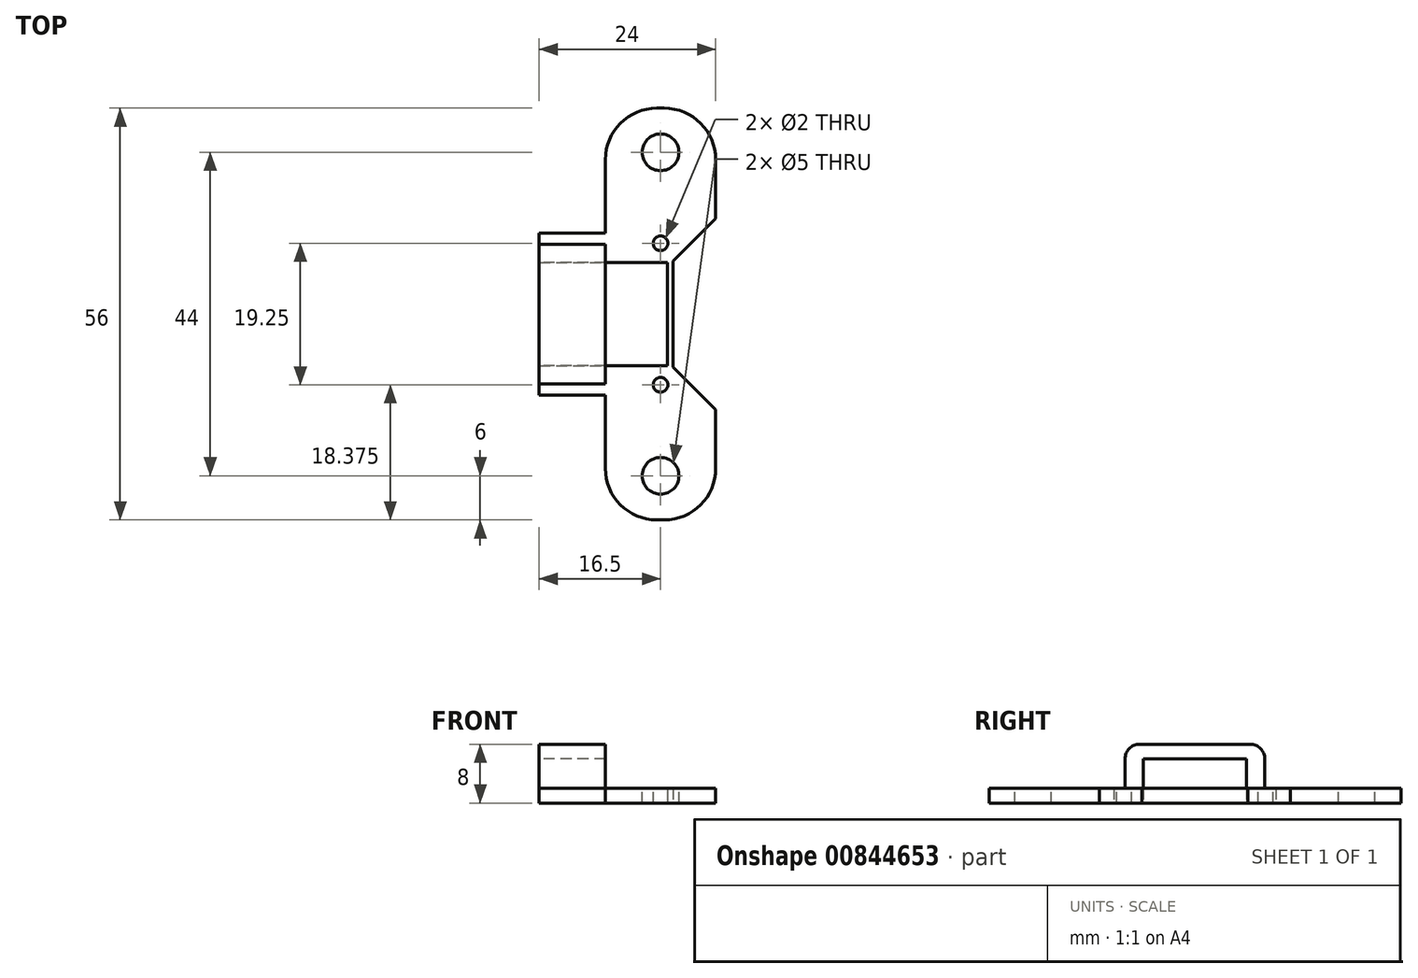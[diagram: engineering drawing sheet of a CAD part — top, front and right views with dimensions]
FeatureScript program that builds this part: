
annotation { "Feature Type Name" : "Feature", "Feature Type Description" : "" }
export const myFeature = defineFeature(function(context is Context, id is Id, definition is map)
    precondition{}
    {
        {
            var Q0;
            Q0=qCreatedBy(makeId("Top.planeOp"),FACE);
            var sketch = newSketch(context, id + "F0", { "sketchPlane" : qUnion([Q0])});
            skLineSegment(sketch, "E0.bottom", {"start": v(-7.5, 10.5) * mm, "end": v(7.5, 10.5) * mm});
            skLineSegment(sketch, "E0.top", {"start": v(-7.5, -10.5) * mm, "end": v(7.5, -10.5) * mm});
            skLineSegment(sketch, "E0.left", {"start": v(-7.5, 10.5) * mm, "end": v(-7.5, -10.5) * mm});
            skLineSegment(sketch, "E0.right", {"start": v(7.5, 10.5) * mm, "end": v(7.5, -10.5) * mm});
            skPoint(sketch, "E0.middle", {"position": v(0, 0) * mm});
            skLineSegment(sketch, "E1", {"start": v(16.54, 17.5) * mm, "end": v(-27.39, 17.5) * mm});
            skLineSegment(sketch, "E2", {"start": v(-2.72, 10.5) * mm, "end": v(-2.52, 10.5) * mm});
            skLineSegment(sketch, "E3", {"start": v(-2.72, 11.06) * mm, "end": v(-1.72, 10.5) * mm});
            skLineSegment(sketch, "E4.MirrorCS", {"start": v(-2.72, 23.94) * mm, "end": v(-1.72, 24.5) * mm});
            skLineSegment(sketch, "E5.MirrorCS", {"start": v(-2.72, 24.5) * mm, "end": v(-2.52, 24.5) * mm});
            skPoint(sketch, "E6.MirrorP", {"position": v(0, 35) * mm});
            skLineSegment(sketch, "E7.MirrorCS", {"start": v(-7.5, 45.5) * mm, "end": v(7.5, 45.5) * mm});
            skLineSegment(sketch, "E8.MirrorCS", {"start": v(-7.5, 24.5) * mm, "end": v(7.5, 24.5) * mm});
            skLineSegment(sketch, "E9.MirrorCS", {"start": v(-7.5, 24.5) * mm, "end": v(-7.5, 45.5) * mm});
            skLineSegment(sketch, "E10.MirrorCS", {"start": v(7.5, 24.5) * mm, "end": v(7.5, 45.5) * mm});
            skLineSegment(sketch, "E11", {"start": v(1.7, 10.5) * mm, "end": v(1.7, 24.5) * mm});
            skLineSegment(sketch, "E12", {"start": v(0.94, 10.5) * mm, "end": v(0.94, 24.5) * mm});
            skSolve(sketch);
        }
        {
            var Q0;
            Q0=qSketchRegion(id+"F0",true);
            extrude(context, id + "F1", {"entities" : qUnion([Q0]), "depth" : 2 * mm, "offsetDistance" : 25 * mm});
        }
        {
            var Q0;
            Q0=makeQuery(id+"F1.opExtrude","SWEPT_EDGE",EDGE,{"disambiguationData":[OSD([sQuery(id+"F0.wireOp",EDGE,"E0.top"),sQuery(id+"F0.wireOp",EDGE,"E0.left")])]});
            var Q1;
            Q1=makeQuery(id+"F1.opExtrude","SWEPT_EDGE",EDGE,{"disambiguationData":[OSD([sQuery(id+"F0.wireOp",EDGE,"E0.top"),sQuery(id+"F0.wireOp",EDGE,"E0.right")])]});
            var Q2;
            Q2=makeQuery(id+"F1.opExtrude","SWEPT_EDGE",EDGE,{"disambiguationData":[OSD([sQuery(id+"F0.wireOp",EDGE,"4d69a73c-c125-441b-aeee-6358f9a7b48c0.MirrorCS"),sQuery(id+"F0.wireOp",EDGE,"4d69a73c-c125-441b-aeee-6358f9a7b48c3.MirrorCS")])]});
            var Q3;
            Q3=makeQuery(id+"F1.opExtrude","SWEPT_EDGE",EDGE,{"disambiguationData":[OSD([sQuery(id+"F0.wireOp",EDGE,"4d69a73c-c125-441b-aeee-6358f9a7b48c1.MirrorCS"),sQuery(id+"F0.wireOp",EDGE,"4d69a73c-c125-441b-aeee-6358f9a7b48c3.MirrorCS")])]});
            var Q4;
            Q4=makeQuery(id+"F1.opExtrude","SWEPT_EDGE",EDGE,{"disambiguationData":[OSD([sQuery(id+"F0.wireOp",EDGE,"E7.MirrorCS"),sQuery(id+"F0.wireOp",EDGE,"E10.MirrorCS")])]});
            var Q5;
            Q5=makeQuery(id+"F1.opExtrude","SWEPT_EDGE",EDGE,{"disambiguationData":[OSD([sQuery(id+"F0.wireOp",EDGE,"E7.MirrorCS"),sQuery(id+"F0.wireOp",EDGE,"E9.MirrorCS")])]});
            fillet(context, id + "F2", {"entities" : qUnion([Q0, Q1, Q2, Q3, Q4, Q5]), "radius" : 7 * mm, "tangentPropagation" : true, "allowEdgeOverflow" : false});
        }
        {
            var Q0;
            Q0=makeQuery(id+"F1.opExtrude","CAP_FACE",FACE,{"disambiguationData":[OSD([sQuery(id+"F0.wireOp",EDGE,"E0.bottom"),sQuery(id+"F0.wireOp",EDGE,"E0.top"),sQuery(id+"F0.wireOp",EDGE,"E0.left"),sQuery(id+"F0.wireOp",EDGE,"E0.right")])],"isStart":false});
            var sketch = newSketch(context, id + "F3", { "sketchPlane" : qUnion([Q0])});
            skCircle(sketch, "E13", {"center": v(0, -4.5) * mm, "radius": 2.5 * mm});
            skLineSegment(sketch, "E14", {"start": v(0, -10.5) * mm, "end": v(0, -4.5) * mm});
            skLineSegment(sketch, "E15", {"start": v(4.6, 10.5) * mm, "end": v(4.6, 17) * mm});
            skLineSegment(sketch, "E16", {"start": v(19.61, 17) * mm, "end": v(-16.13, 17) * mm});
            skLineSegment(sketch, "E17", {"start": v(0, -4.5) * mm, "end": v(0, 7.87) * mm});
            skCircle(sketch, "E18", {"center": v(0, 7.87) * mm, "radius": 1 * mm});
            skLineSegment(sketch, "E19", {"start": v(0, 45.5) * mm, "end": v(0, 39.5) * mm});
            skCircle(sketch, "E20", {"center": v(0, 39.5) * mm, "radius": 2.5 * mm});
            skLineSegment(sketch, "E21", {"start": v(0, 39.5) * mm, "end": v(0, 27.12) * mm});
            skCircle(sketch, "E22", {"center": v(0, 27.12) * mm, "radius": 1 * mm});
            skSolve(sketch);
        }
        {
            var Q0;
            Q0=qSketchRegion(id+"F3",true);
            extrude(context, id + "F4", {"entities" : qUnion([Q0]), "operationType" : NewBodyOperationType.REMOVE, "endBound" : BoundingType.UP_TO_NEXT, "oppositeDirection" : true, "depth" : 25 * mm, "offsetDistance" : 25 * mm});
        }
        {
            var Q0;
            Q0=makeQuery(id+"F1.opExtrude","SWEPT_FACE",FACE,{"disambiguationData":[OSD([sQuery(id+"F0.wireOp",EDGE,"E0.left")])]});
            var sketch = newSketch(context, id + "F5", { "sketchPlane" : qUnion([Q0])});
            skLineSegment(sketch, "E23.bottom", {"start": v(-10.5, 2) * mm, "end": v(-6.5, 2) * mm});
            skLineSegment(sketch, "E23.top", {"start": v(-10.5, 0) * mm, "end": v(-6.5, 0) * mm});
            skLineSegment(sketch, "E23.left", {"start": v(-10.5, 2) * mm, "end": v(-10.5, 0) * mm});
            skLineSegment(sketch, "E23.right", {"start": v(-6.5, 2) * mm, "end": v(-6.5, 0) * mm});
            skSolve(sketch);
        }
        {
            var Q0;
            Q0=makeQuery(id+"F5.imprint","IMPRINT",FACE,{"disambiguationData":[TD([[makeQuery(id+"F5.imprint","IMPRINT",EDGE,{"derivedFrom":sQuery(id+"F5.wireOp",EDGE,"E23.bottom")}),-1.0]])]});
            var Q1;
            Q1=makeQuery(id+"F5.imprint","IMPRINT",FACE,{"disambiguationData":[TD([[makeQuery(id+"F5.imprint","IMPRINT",EDGE,{"derivedFrom":sQuery(id+"F5.wireOp",EDGE,"b54e5eb9-cc67-4eb8-8262-082db1211d390.MirrorCS")}),-1.0]])]});
            extrude(context, id + "F6", {"entities" : qUnion([Q0, Q1]), "operationType" : NewBodyOperationType.ADD, "depth" : 9 * mm, "offsetDistance" : 25 * mm});
        }
        {
            var Q0;
            Q0=makeQuery(id+"F6.boolean.opBoolean","MERGE",FACE,{"derivedFrom":[makeQuery(id+"F1.opExtrude","CAP_FACE",FACE,{"disambiguationData":[OSD([sQuery(id+"F0.wireOp",EDGE,"E0.bottom"),sQuery(id+"F0.wireOp",EDGE,"E0.top"),sQuery(id+"F0.wireOp",EDGE,"E0.left"),sQuery(id+"F0.wireOp",EDGE,"E0.right")])],"isStart":false}),makeQuery(id+"F6.opExtrude","SWEPT_FACE",FACE,{"disambiguationData":[OSD([sQuery(id+"F5.wireOp",EDGE,"E23.bottom")])]})]});
            var sketch = newSketch(context, id + "F7", { "sketchPlane" : qUnion([Q0])});
            skLineSegment(sketch, "E24.bottom", {"start": v(-16.5, 10.5) * mm, "end": v(-7.5, 10.5) * mm});
            skLineSegment(sketch, "E24.top", {"start": v(-16.5, 8) * mm, "end": v(-7.5, 8) * mm});
            skLineSegment(sketch, "E24.left", {"start": v(-16.5, 10.5) * mm, "end": v(-16.5, 8) * mm});
            skLineSegment(sketch, "E24.right", {"start": v(-7.5, 10.5) * mm, "end": v(-7.5, 8) * mm});
            skLineSegment(sketch, "E25", {"start": v(-8.07, 10.5) * mm, "end": v(-8.07, 17) * mm});
            skLineSegment(sketch, "E26", {"start": v(-3.29, 17) * mm, "end": v(-20.76, 17) * mm});
            skSolve(sketch);
        }
        {
            var Q0;
            Q0=makeQuery(id+"F7.imprint","IMPRINT",FACE,{"disambiguationData":[TD([[makeQuery(id+"F7.imprint","IMPRINT",EDGE,{"derivedFrom":sQuery(id+"F7.wireOp",EDGE,"E24.bottom")}),-1.0]])]});
            var Q1;
            Q1=makeQuery(id+"F7.imprint","IMPRINT",FACE,{"disambiguationData":[TD([[makeQuery(id+"F7.imprint","IMPRINT",EDGE,{"derivedFrom":sQuery(id+"F7.wireOp",EDGE,"8816faac-e9ce-4b0a-a729-0d2c297b35d70.MirrorCS")}),1.0]])]});
            extrude(context, id + "F8", {"entities" : qUnion([Q0, Q1]), "operationType" : NewBodyOperationType.ADD, "depth" : 6 * mm, "offsetDistance" : 25 * mm});
        }
        {
            var Q0;
            Q0=makeQuery(id+"F8.boolean.opBoolean","MERGE",FACE,{"derivedFrom":[makeQuery(id+"F6.boolean.opBoolean","MERGE",FACE,{"derivedFrom":[makeQuery(id+"F1.opExtrude","SWEPT_FACE",FACE,{"disambiguationData":[OSD([sQuery(id+"F0.wireOp",EDGE,"E0.bottom")])]}),makeQuery(id+"F6.opExtrude","SWEPT_FACE",FACE,{"disambiguationData":[OSD([sQuery(id+"F5.wireOp",EDGE,"E23.left")])]})]}),makeQuery(id+"F8.opExtrude","SWEPT_FACE",FACE,{"disambiguationData":[OSD([sQuery(id+"F7.wireOp",EDGE,"E24.bottom")])]})]});
            var sketch = newSketch(context, id + "F9", { "sketchPlane" : qUnion([Q0])});
            skLineSegment(sketch, "E27.bottom", {"start": v(7.5, 8) * mm, "end": v(16.5, 8) * mm});
            skLineSegment(sketch, "E27.top", {"start": v(7.5, 6) * mm, "end": v(16.5, 6) * mm});
            skLineSegment(sketch, "E27.left", {"start": v(7.5, 8) * mm, "end": v(7.5, 6) * mm});
            skLineSegment(sketch, "E27.right", {"start": v(16.5, 8) * mm, "end": v(16.5, 6) * mm});
            skSolve(sketch);
        }
        {
            var Q0;
            Q0 = qSketchRegion(id + "F9", true);
            extrude(context, id + "F10", {"entities" : qUnion([Q0]), "operationType" : NewBodyOperationType.ADD, "depth" : 14 * mm, "offsetDistance" : 25 * mm});
        }
        {
            var Q0;
            Q0=makeQuery(id+"F1.opExtrude","SWEPT_FACE",FACE,{"disambiguationData":[OSD([sQuery(id+"F0.wireOp",EDGE,"E9.MirrorCS")])]});
            var sketch = newSketch(context, id + "F11", { "sketchPlane" : qUnion([Q0])});
            skLineSegment(sketch, "E28.bottom", {"start": v(-24.5, 2) * mm, "end": v(-28.5, 2) * mm});
            skLineSegment(sketch, "E28.top", {"start": v(-24.5, 0) * mm, "end": v(-28.5, 0) * mm});
            skLineSegment(sketch, "E28.left", {"start": v(-24.5, 2) * mm, "end": v(-24.5, 0) * mm});
            skLineSegment(sketch, "E28.right", {"start": v(-28.5, 2) * mm, "end": v(-28.5, 0) * mm});
            skSolve(sketch);
        }
        {
            var Q0;
            Q0=makeQuery(id+"F11.imprint","IMPRINT",FACE,{"disambiguationData":[TD([[makeQuery(id+"F11.imprint","IMPRINT",EDGE,{"derivedFrom":sQuery(id+"F11.wireOp",EDGE,"E28.bottom")}),1.0]])]});
            extrude(context, id + "F12", {"entities" : qUnion([Q0]), "operationType" : NewBodyOperationType.ADD, "depth" : 9 * mm, "offsetDistance" : 25 * mm});
        }
        {
            var Q0;
            Q0=makeQuery(id+"F12.boolean.opBoolean","MERGE",FACE,{"derivedFrom":[makeQuery(id+"F6.boolean.opBoolean","MERGE",FACE,{"derivedFrom":[makeQuery(id+"F1.opExtrude","CAP_FACE",FACE,{"disambiguationData":[OSD([sQuery(id+"F0.wireOp",EDGE,"E0.bottom"),sQuery(id+"F0.wireOp",EDGE,"E0.top"),sQuery(id+"F0.wireOp",EDGE,"E0.left"),sQuery(id+"F0.wireOp",EDGE,"E0.right"),sQuery(id+"F0.wireOp",EDGE,"4d69a73c-c125-441b-aeee-6358f9a7b48c0.MirrorCS"),sQuery(id+"F0.wireOp",EDGE,"4d69a73c-c125-441b-aeee-6358f9a7b48c1.MirrorCS"),sQuery(id+"F0.wireOp",EDGE,"4d69a73c-c125-441b-aeee-6358f9a7b48c2.MirrorCS"),sQuery(id+"F0.wireOp",EDGE,"4d69a73c-c125-441b-aeee-6358f9a7b48c3.MirrorCS"),sQuery(id+"F0.wireOp",EDGE,"g9jlqCbB-dlW6-GfCL-Cnde-qGy19OqoHRY9"),sQuery(id+"F0.wireOp",EDGE,"YbJINRbM-a1Qn-wjUW-cin5-VxgVwcj2AwoP")])],"isStart":false}),makeQuery(id+"F6.opExtrude","SWEPT_FACE",FACE,{"disambiguationData":[OSD([sQuery(id+"F5.wireOp",EDGE,"E23.bottom")])]})]}),makeQuery(id+"F12.opExtrude","SWEPT_FACE",FACE,{"disambiguationData":[OSD([sQuery(id+"F11.wireOp",EDGE,"fP8b6zdj-eh1C-UePH-MVhF-EP79czhgLk8B.bottom")])]})]});
            var sketch = newSketch(context, id + "F13", { "sketchPlane" : qUnion([Q0])});
            skLineSegment(sketch, "E29.bottom", {"start": v(-16.5, 24.5) * mm, "end": v(-7.5, 24.5) * mm});
            skLineSegment(sketch, "E29.top", {"start": v(-16.5, 27) * mm, "end": v(-7.5, 27) * mm});
            skLineSegment(sketch, "E29.left", {"start": v(-16.5, 24.5) * mm, "end": v(-16.5, 27) * mm});
            skLineSegment(sketch, "E29.right", {"start": v(-7.5, 24.5) * mm, "end": v(-7.5, 27) * mm});
            skSolve(sketch);
        }
        {
            var Q0;
            Q0=makeQuery(id+"F13.imprint","IMPRINT",FACE,{"disambiguationData":[TD([[makeQuery(id+"F13.imprint","IMPRINT",EDGE,{"derivedFrom":sQuery(id+"F13.wireOp",EDGE,"E29.bottom")}),1.0]])]});
            extrude(context, id + "F14", {"entities" : qUnion([Q0]), "operationType" : NewBodyOperationType.ADD, "depth" : 6 * mm, "offsetDistance" : 25 * mm});
        }
        {
            var Q0;
            Q0=makeQuery(id+"F1.opExtrude","SWEPT_EDGE",EDGE,{"disambiguationData":[OSD([sQuery(id+"F0.wireOp",EDGE,"4d69a73c-c125-441b-aeee-6358f9a7b48c0.MirrorCS"),sQuery(id+"F0.wireOp",EDGE,"4d69a73c-c125-441b-aeee-6358f9a7b48c2.MirrorCS")])]});
            var Q1;
            Q1=makeQuery(id+"F1.opExtrude","SWEPT_EDGE",EDGE,{"disambiguationData":[OSD([sQuery(id+"F0.wireOp",EDGE,"E0.bottom"),sQuery(id+"F0.wireOp",EDGE,"E0.right")])]});
            var Q2;
            Q2=makeQuery(id+"F1.opExtrude","SWEPT_EDGE",EDGE,{"disambiguationData":[OSD([sQuery(id+"F0.wireOp",EDGE,"E8.MirrorCS"),sQuery(id+"F0.wireOp",EDGE,"E10.MirrorCS")])]});
            chamfer(context, id + "F15", {"entities" : qUnion([Q0, Q1, Q2]), "width" : 6 * mm, "tangentPropagation" : true});
        }
        {
            var Q0;
            Q0=makeQuery(id+"F14.opExtrude","CAP_EDGE",EDGE,{"disambiguationData":[OSD([sQuery(id+"F13.wireOp",EDGE,"2s9bTL7p-TM7B-V0Ax-Icok-Ozjgmq8opogu.top")])],"isStart":true});
            var Q1;
            Q1=makeQuery(id+"F8.opExtrude","CAP_EDGE",EDGE,{"disambiguationData":[OSD([sQuery(id+"F7.wireOp",EDGE,"E24.top")])],"isStart":true});
            var Q2;
            Q2=makeQuery(id+"F8.opExtrude","CAP_EDGE",EDGE,{"disambiguationData":[OSD([sQuery(id+"F7.wireOp",EDGE,"E24.top")])],"isStart":false});
            var Q3;
            Q3=makeQuery(id+"F14.opExtrude","CAP_EDGE",EDGE,{"disambiguationData":[OSD([sQuery(id+"F13.wireOp",EDGE,"2s9bTL7p-TM7B-V0Ax-Icok-Ozjgmq8opogu.top")])],"isStart":false});
            var Q4;
            Q4=makeQuery(id+"F14.opExtrude","CAP_EDGE",EDGE,{"disambiguationData":[OSD([sQuery(id+"F13.wireOp",EDGE,"E29.top")])],"isStart":false});
            var Q5;
            Q5=makeQuery(id+"F14.opExtrude","CAP_EDGE",EDGE,{"disambiguationData":[OSD([sQuery(id+"F13.wireOp",EDGE,"E29.top")])],"isStart":true});
            fillet(context, id + "F16", {"entities" : qUnion([Q0, Q1, Q2, Q3, Q4, Q5]), "radius" : 2 * mm, "tangentPropagation" : true, "allowEdgeOverflow" : false});
        }
    });
